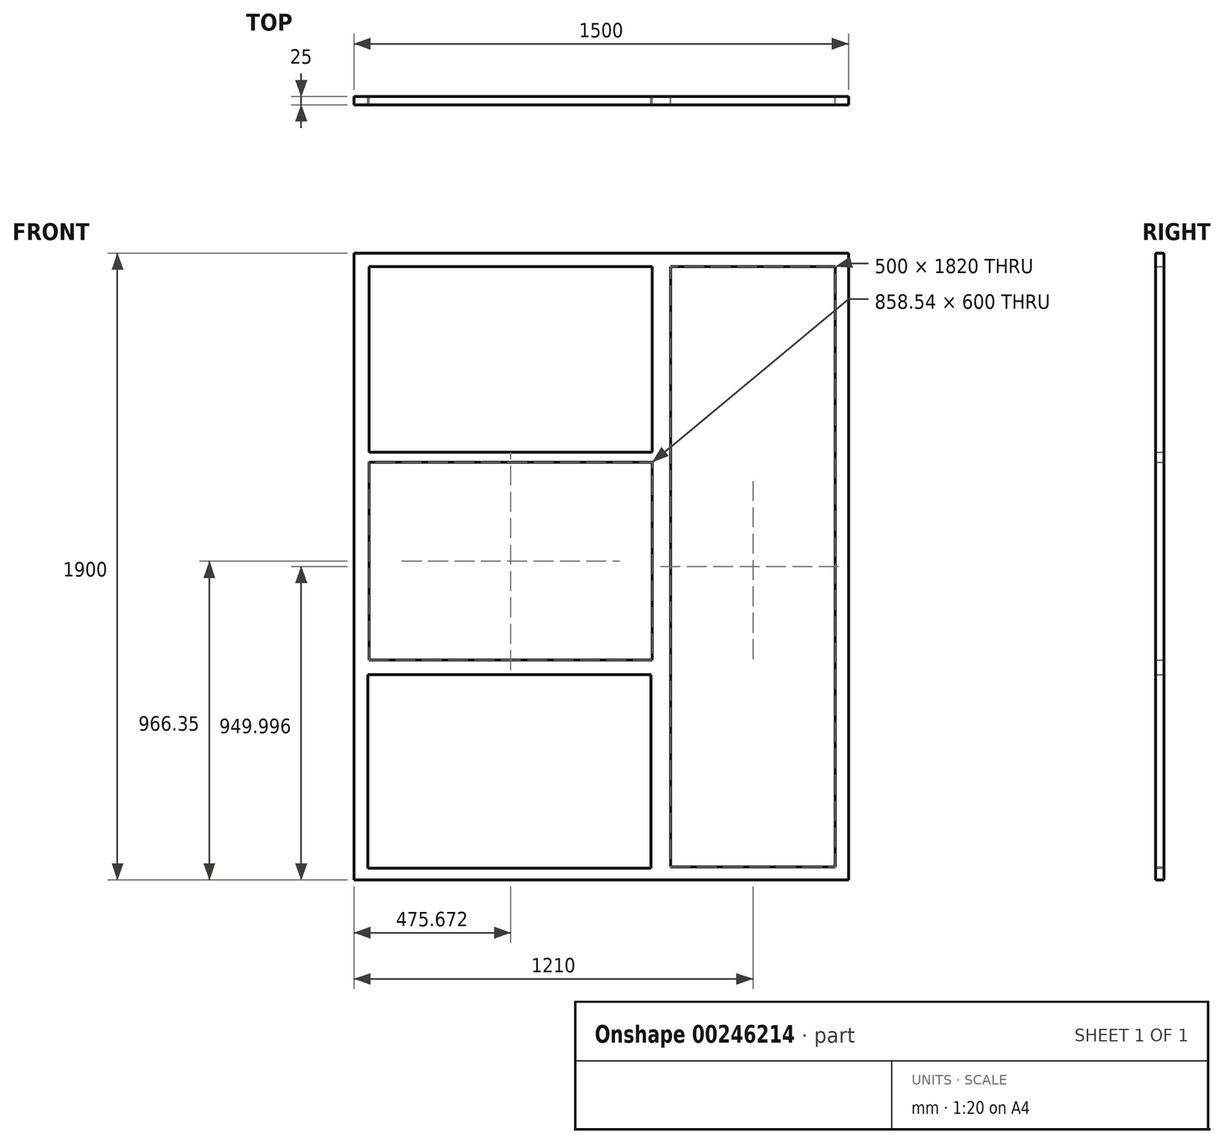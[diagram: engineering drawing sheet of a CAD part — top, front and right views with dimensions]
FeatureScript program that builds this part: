
annotation { "Feature Type Name" : "Feature", "Feature Type Description" : "" }
export const myFeature = defineFeature(function(context is Context, id is Id, definition is map)
    precondition{}
    {
        {
            var Q0;
            Q0=qCreatedBy(makeId("Front.planeOp"),FACE);
            var sketch = newSketch(context, id + "F0", { "sketchPlane" : qUnion([Q0])});
            skLineSegment(sketch, "E0.bottom", {"start": v(-765.44, 1394.37) * mm, "end": v(734.56, 1394.37) * mm});
            skLineSegment(sketch, "E0.top", {"start": v(-765.44, -505.63) * mm, "end": v(734.56, -505.63) * mm});
            skLineSegment(sketch, "E0.left", {"start": v(-765.44, 1394.37) * mm, "end": v(-765.44, -505.63) * mm});
            skLineSegment(sketch, "E0.right", {"start": v(734.56, 1394.37) * mm, "end": v(734.56, -505.63) * mm});
            skLineSegment(sketch, "E1.bottom", {"start": v(694.56, 1354.37) * mm, "end": v(194.56, 1354.37) * mm});
            skLineSegment(sketch, "E1.top", {"start": v(694.56, -465.63) * mm, "end": v(194.56, -465.63) * mm});
            skLineSegment(sketch, "E1.left", {"start": v(694.56, 1354.37) * mm, "end": v(694.56, -465.63) * mm});
            skLineSegment(sketch, "E1.right", {"start": v(194.56, 1354.37) * mm, "end": v(194.56, -465.63) * mm});
            skLineSegment(sketch, "E2.bottom", {"start": v(-719.04, 1354.37) * mm, "end": v(138.74, 1354.37) * mm});
            skLineSegment(sketch, "E2.top", {"start": v(-719.04, 791.3) * mm, "end": v(138.74, 791.3) * mm});
            skLineSegment(sketch, "E2.left", {"start": v(-719.04, 1354.37) * mm, "end": v(-719.04, 791.3) * mm});
            skLineSegment(sketch, "E2.right", {"start": v(138.74, 1354.37) * mm, "end": v(138.74, 791.3) * mm});
            skLineSegment(sketch, "E3.bottom", {"start": v(-719.04, 760.72) * mm, "end": v(139.5, 760.72) * mm});
            skLineSegment(sketch, "E3.top", {"start": v(-719.04, 160.72) * mm, "end": v(139.5, 160.72) * mm});
            skLineSegment(sketch, "E3.left", {"start": v(-719.04, 760.72) * mm, "end": v(-719.04, 160.72) * mm});
            skLineSegment(sketch, "E3.right", {"start": v(139.5, 760.72) * mm, "end": v(139.5, 160.72) * mm});
            skLineSegment(sketch, "E4.bottom", {"start": v(-723.03, -469.85) * mm, "end": v(135.24, -469.85) * mm});
            skLineSegment(sketch, "E4.top", {"start": v(-723.03, 116.93) * mm, "end": v(135.24, 116.93) * mm});
            skLineSegment(sketch, "E4.left", {"start": v(-723.03, -469.85) * mm, "end": v(-723.03, 116.93) * mm});
            skLineSegment(sketch, "E4.right", {"start": v(135.24, -469.85) * mm, "end": v(135.24, 116.93) * mm});
            skSolve(sketch);
        }
        {
            var Q0;
            Q0=makeQuery(id+"F0.imprint","IMPRINT",FACE,{"disambiguationData":[TD([[makeQuery(id+"F0.imprint","IMPRINT",EDGE,{"derivedFrom":sQuery(id+"F0.wireOp",EDGE,"E0.bottom")}),-1.0]])]});
            extrude(context, id + "F1", {"entities" : qUnion([Q0]), "depth" : 25 * mm});
        }
    });
